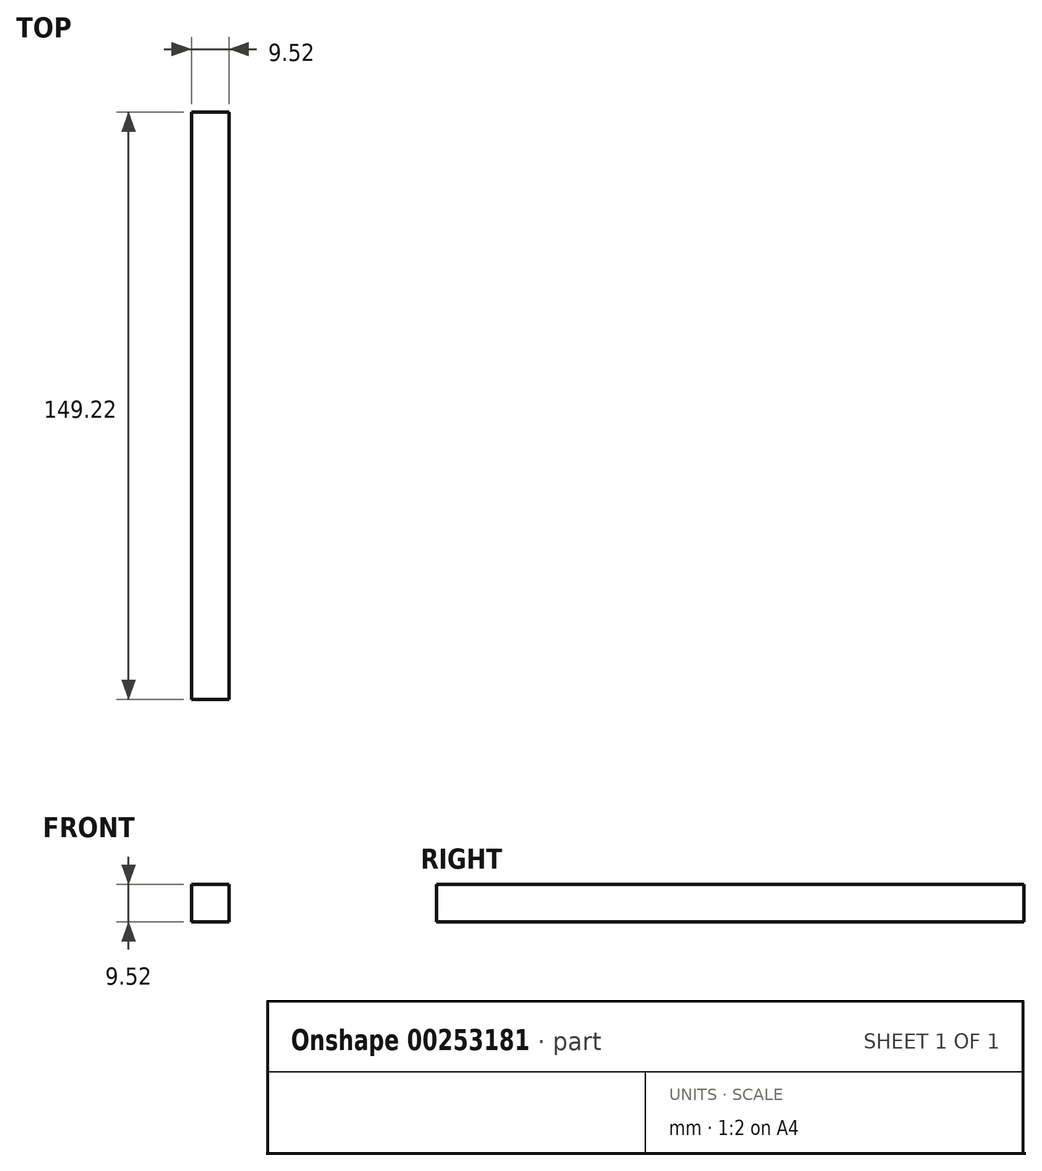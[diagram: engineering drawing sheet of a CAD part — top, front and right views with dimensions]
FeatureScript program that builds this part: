
annotation { "Feature Type Name" : "Feature", "Feature Type Description" : "" }
export const myFeature = defineFeature(function(context is Context, id is Id, definition is map)
    precondition{}
    {
        {
            var Q0;
            Q0=qCreatedBy(makeId("Front.planeOp"),FACE);
            var sketch = newSketch(context, id + "F0", { "sketchPlane" : qUnion([Q0])});
            skLineSegment(sketch, "E0.rect.bottom", {"start": v(-4.76, -4.76) * mm, "end": v(4.76, -4.76) * mm});
            skLineSegment(sketch, "E0.rect.top", {"start": v(-4.76, 4.76) * mm, "end": v(4.76, 4.76) * mm});
            skLineSegment(sketch, "E0.rect.left", {"start": v(-4.76, -4.76) * mm, "end": v(-4.76, 4.76) * mm});
            skLineSegment(sketch, "E0.rect.right", {"start": v(4.76, -4.76) * mm, "end": v(4.76, 4.76) * mm});
            skPoint(sketch, "E0.rect.middle", {"position": v(0, 0) * mm});
            skSolve(sketch);
        }
        {
            var Q0;
            Q0=makeQuery(id+"F0.imprint","IMPRINT",FACE,{"disambiguationData":[TD([[makeQuery(id+"F0.imprint","IMPRINT",EDGE,{"derivedFrom":sQuery(id+"F0.wireOp",EDGE,"E0.rect.bottom")}),1.0]])]});
            extrude(context, id + "F1", {"entities" : qUnion([Q0]), "depth" : 149.22 * mm, "symmetric" : true});
        }
    });
